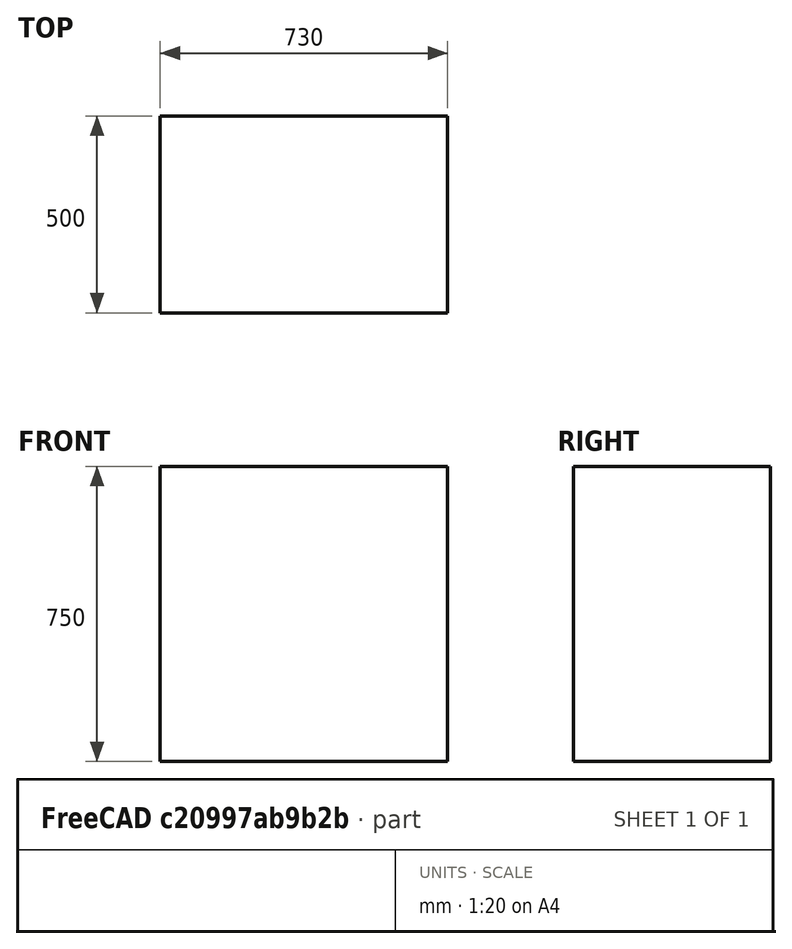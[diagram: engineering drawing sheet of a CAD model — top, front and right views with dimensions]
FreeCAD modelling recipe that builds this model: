
FCSTD DOCUMENT  (FreeCAD 1.0R38806 (Git))
Label: above_table
License: All rights reserved
LicenseURL: https://en.wikipedia.org/wiki/All_rights_reserved
objects: Sketcher::SketchObject×2, Part::Box×1, Part::Extrusion×1
note: 6 computed .brp shape members not serialized (recipe doc carries the construction recipe); baked Part::Feature solids carry a one-line shape summary decoded from their .brp

FEATURE [Sketcher::SketchObject] Sketch001  label="side_view"
  ArcFitTolerance = 1e-06
  FullyConstrained = true
  MakeInternals = false
  Placement = pos=(-365,0,0) rot=(1,1,1;2.0944rad)
  sketch-geometry (5):
    g0: LineSegment StartX=-250 StartY=-375 StartZ=0 EndX=250 EndY=-375 EndZ=0
    g1: LineSegment StartX=250 StartY=-375 StartZ=0 EndX=250 EndY=375 EndZ=0
    g2: LineSegment StartX=250 StartY=375 StartZ=0 EndX=-250 EndY=375 EndZ=0
    g3: LineSegment StartX=-250 StartY=375 StartZ=0 EndX=-250 EndY=-375 EndZ=0
    g4: GeomPoint [constr] X=0 Y=0 Z=0
  constraints (12):
    c: Coincident(g0,g1)
    c: Coincident(g1,g2)
    c: Coincident(g2,g3)
    c: Coincident(g3,g0)
    c: Horizontal(g0)
    c: Horizontal(g2)
    c: Vertical(g1)
    c: Vertical(g3)
    c: Symmetric(g2,g0,g4)
    c: Distance(g1,g3) = 500
    c: Distance(g0,g2) = 750
    c: Coincident(g4,g-1)
FEATURE [Sketcher::SketchObject] Sketch002  label="front_view"
  ArcFitTolerance = 1e-06
  FullyConstrained = false
  MakeInternals = false
  Placement = pos=(0,-240,0) rot=(58,0.57735,0.57735;1.5708rad)
  sketch-geometry (14):
    g0: LineSegment StartX=365 StartY=-384.168 StartZ=0 EndX=365 EndY=375 EndZ=0
    g1: LineSegment StartX=365 StartY=375 StartZ=0 EndX=-365 EndY=375 EndZ=0
    g2: LineSegment StartX=-365 StartY=375 StartZ=0 EndX=-365 EndY=-375 EndZ=0
    g3: GeomPoint [constr] X=0 Y=0 Z=0
    g4: LineSegment StartX=-365 StartY=-375 StartZ=0 EndX=-315.003 EndY=-375 EndZ=0
    g5: LineSegment StartX=-315.003 StartY=-375 StartZ=0 EndX=-315.003 EndY=256.732 EndZ=0
    g6: LineSegment StartX=-315.003 StartY=256.732 StartZ=0 EndX=315 EndY=256.732 EndZ=0
    g7: LineSegment StartX=315 StartY=256.732 StartZ=0 EndX=315 EndY=-384.168 EndZ=0
    g8: LineSegment StartX=315 StartY=-384.168 StartZ=0 EndX=365 EndY=-384.168 EndZ=0
    g9: LineSegment StartX=-315.003 StartY=256.732 StartZ=0 EndX=-315.003 EndY=329.258 EndZ=0
    g10: LineSegment StartX=-315.003 StartY=329.258 StartZ=0 EndX=315 EndY=329.258 EndZ=0
    g11: LineSegment StartX=315 StartY=329.258 StartZ=0 EndX=315 EndY=256.732 EndZ=0
    g12: LineSegment [constr] StartX=315 StartY=-365.339 StartZ=0 EndX=365 EndY=-365.339 EndZ=0
    g13: LineSegment [constr] StartX=315 StartY=174.316 StartZ=0 EndX=365 EndY=174.316 EndZ=0
  constraints (34):
    c: Coincident(g0,g1)
    c: Coincident(g1,g2)
    c: Horizontal(g1)
    c: Vertical(g0)
    c: Vertical(g2)
    c: Symmetric(g1,g2,g3)
    c: Distance(g2,g1) = 750
    c: Coincident(g3,g-1)
    c: DistanceX(g1,g1) = 730
    c: Coincident(g2,g4)
    c: Horizontal(g4)
    c: Coincident(g4,g5)
    c: Vertical(g5)
    c: Coincident(g5,g6)
    c: Horizontal(g6)
    c: Coincident(g6,g7)
    c: Vertical(g7)
    c: Coincident(g7,g8)
    c: Coincident(g8,g0)
    c: Distance(g4,g4) = 49.997
    c: DistanceX(g8,g8) = 50
    c: Coincident(g5,g9)
    c: Vertical(g9)
    c: Coincident(g9,g10)
    c: Horizontal(g10)
    c: Coincident(g10,g11)
    c: Coincident(g11,g6)
    c: Vertical(g11)
    c: PointOnObject(g12,g7)
    c: PointOnObject(g12,g0)
    c: Horizontal(g12)
    c: PointOnObject(g13,g7)
    c: PointOnObject(g13,g0)
    c: Horizontal(g13)
FEATURE [Part::Box] Box  label="Cube"
  AttacherType = Attacher::AttachEngine3D
  Height = 750
  Length = 730
  Placement = pos=(-365,-217,-376) rot=(0,0,1;0rad)
  Width = 500
FEATURE [Part::Extrusion] Extrude002
  Base = -> Sketch002
  Dir = (0.0199057,-0.999802,9.90688e-05)
  DirMode = 2
  FaceMakerClass = Part::FaceMakerBullseye
  FaceMakerMode = 3
  LengthFwd = 0
  LengthRev = 550
  Solid = false
  Symmetric = false
